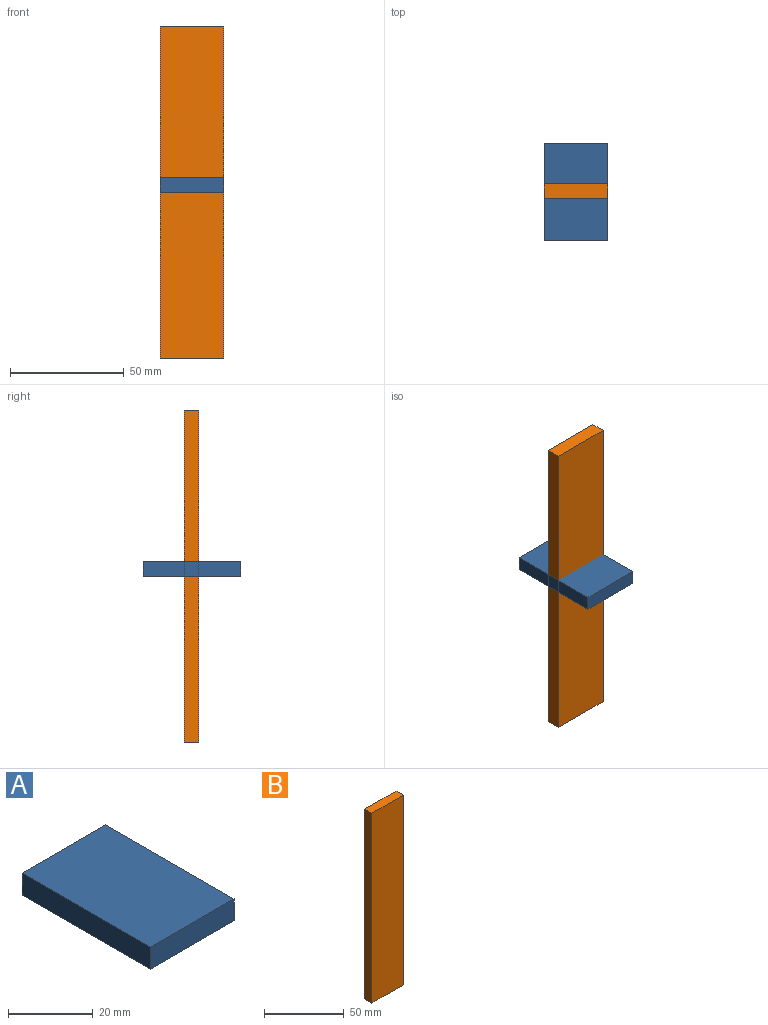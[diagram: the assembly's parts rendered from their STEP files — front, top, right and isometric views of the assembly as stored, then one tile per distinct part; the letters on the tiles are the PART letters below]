
ASSEMBLY  parts=2 mates=1
PART A: 6 faces, bbox 27.9x42.8x6.4 mm
  f0: plane 27.94x6.35mm, normal (0,1,0), area 177.4mm2, adj f1,f3,f4,f5
  f1: plane 42.84x6.35mm, normal (-1,0,0), area 272mm2, adj f0,f2,f4,f5
  f2: plane 27.94x6.35mm, normal (0,-1,0), area 177.4mm2, adj f1,f3,f4,f5
  f3: plane 42.84x6.35mm, normal (1,0,0), area 272mm2, adj f0,f2,f4,f5
  f4: plane 42.84x27.94mm, normal (0,0,1), area 1196.9mm2, adj f0,f1,f2,f3
  f5: plane 42.84x27.94mm, normal (0,0,-1), area 1196.9mm2, adj f0,f1,f2,f3
PART B: 6 faces, bbox 27.9x6.4x146.1 mm
  f0: plane 27.94x6.35mm, normal (0,0,1), area 177.4mm2, adj f1,f3,f4,f5
  f1: plane 146.05x6.35mm, normal (-1,0,0), area 927.4mm2, adj f0,f2,f4,f5
  f2: plane 27.94x6.35mm, normal (0,0,-1), area 177.4mm2, adj f1,f3,f4,f5
  f3: plane 146.05x6.35mm, normal (1,0,0), area 927.4mm2, adj f0,f2,f4,f5
  f4: plane 146.05x27.94mm, normal (0,-1,0), area 4080.6mm2, adj f0,f1,f2,f3
  f5: plane 146.05x27.94mm, normal (0,1,0), area 4080.6mm2, adj f0,f1,f2,f3
PLACE A t=(-7.8,-9.53,29.5)mm
PLACE B t=(-65.15,-56.17,8.91)mm
MATE planar B.f3 <-> A.f3  axis (1,0,0) through (-82.83,-59.35,29.57)mm
